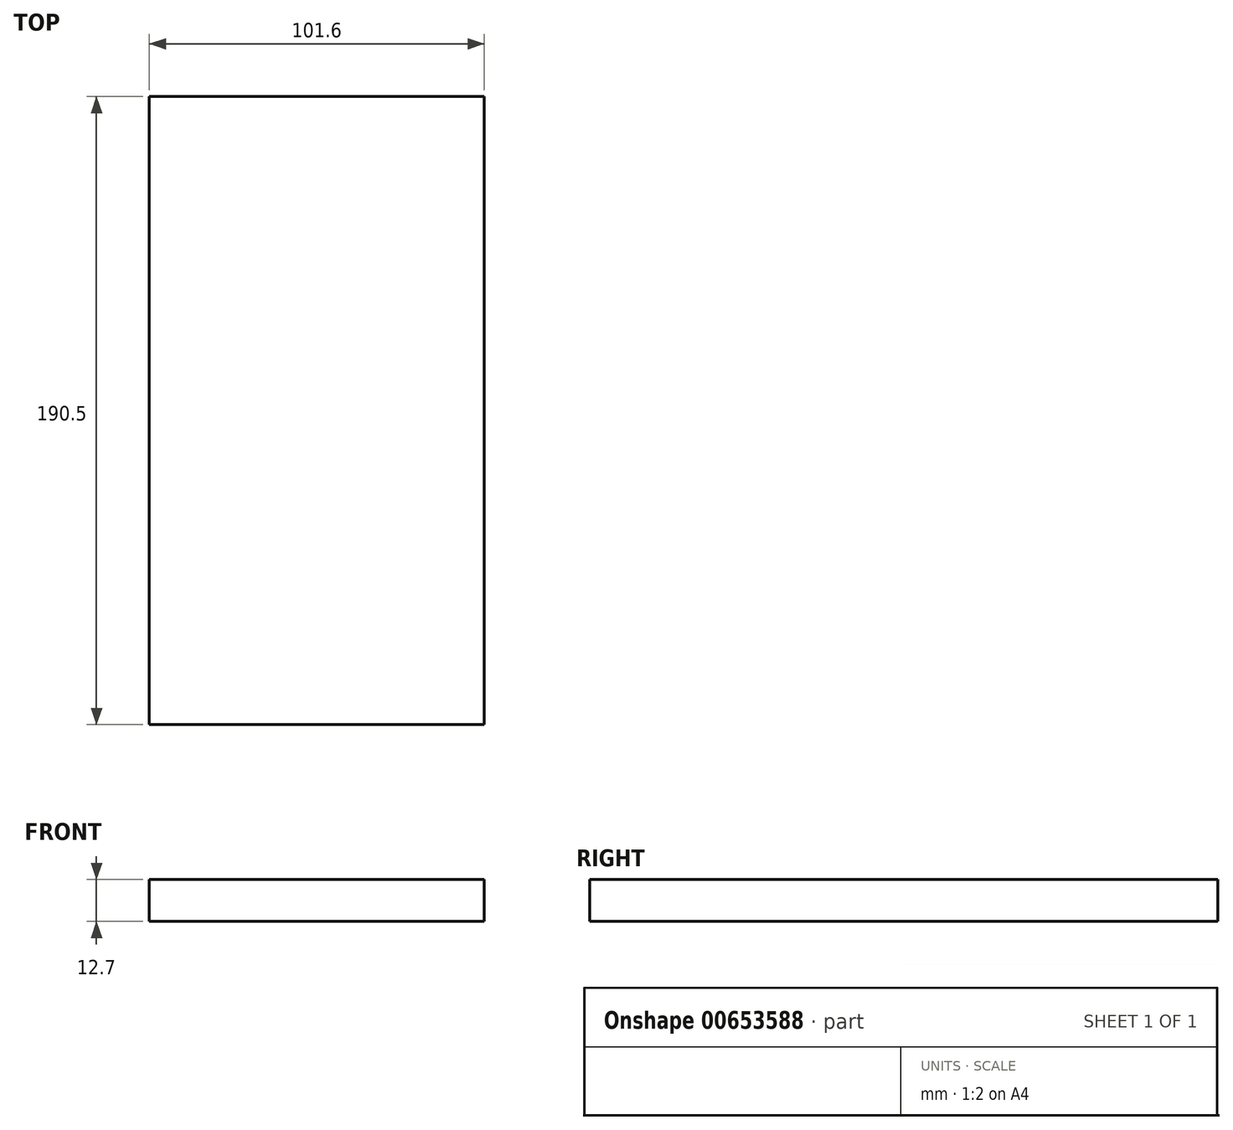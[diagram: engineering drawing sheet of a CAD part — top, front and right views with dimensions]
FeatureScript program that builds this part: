
annotation { "Feature Type Name" : "Feature", "Feature Type Description" : "" }
export const myFeature = defineFeature(function(context is Context, id is Id, definition is map)
    precondition{}
    {
        {
            var Q0;
            Q0=qCreatedBy(makeId("Top.planeOp"),FACE);
            var sketch = newSketch(context, id + "F0", { "sketchPlane" : qUnion([Q0])});
            skLineSegment(sketch, "E0.bottom", {"start": v(50.8, 95.25) * mm, "end": v(-50.8, 95.25) * mm});
            skLineSegment(sketch, "E0.top", {"start": v(50.8, -95.25) * mm, "end": v(-50.8, -95.25) * mm});
            skLineSegment(sketch, "E0.left", {"start": v(50.8, 95.25) * mm, "end": v(50.8, -95.25) * mm});
            skLineSegment(sketch, "E0.right", {"start": v(-50.8, 95.25) * mm, "end": v(-50.8, -95.25) * mm});
            skPoint(sketch, "E0.middle", {"position": v(0, 0) * mm});
            skSolve(sketch);
        }
        {
            var Q0;
            Q0=makeQuery(id+"F0.imprint","IMPRINT",FACE,{"disambiguationData":[TD([[makeQuery(id+"F0.imprint","IMPRINT",EDGE,{"derivedFrom":sQuery(id+"F0.wireOp",EDGE,"E0.bottom")}),1.0]])]});
            extrude(context, id + "F1", {"entities" : qUnion([Q0]), "depth" : 12.7 * mm, "offsetDistance" : 25.4 * mm});
        }
    });
